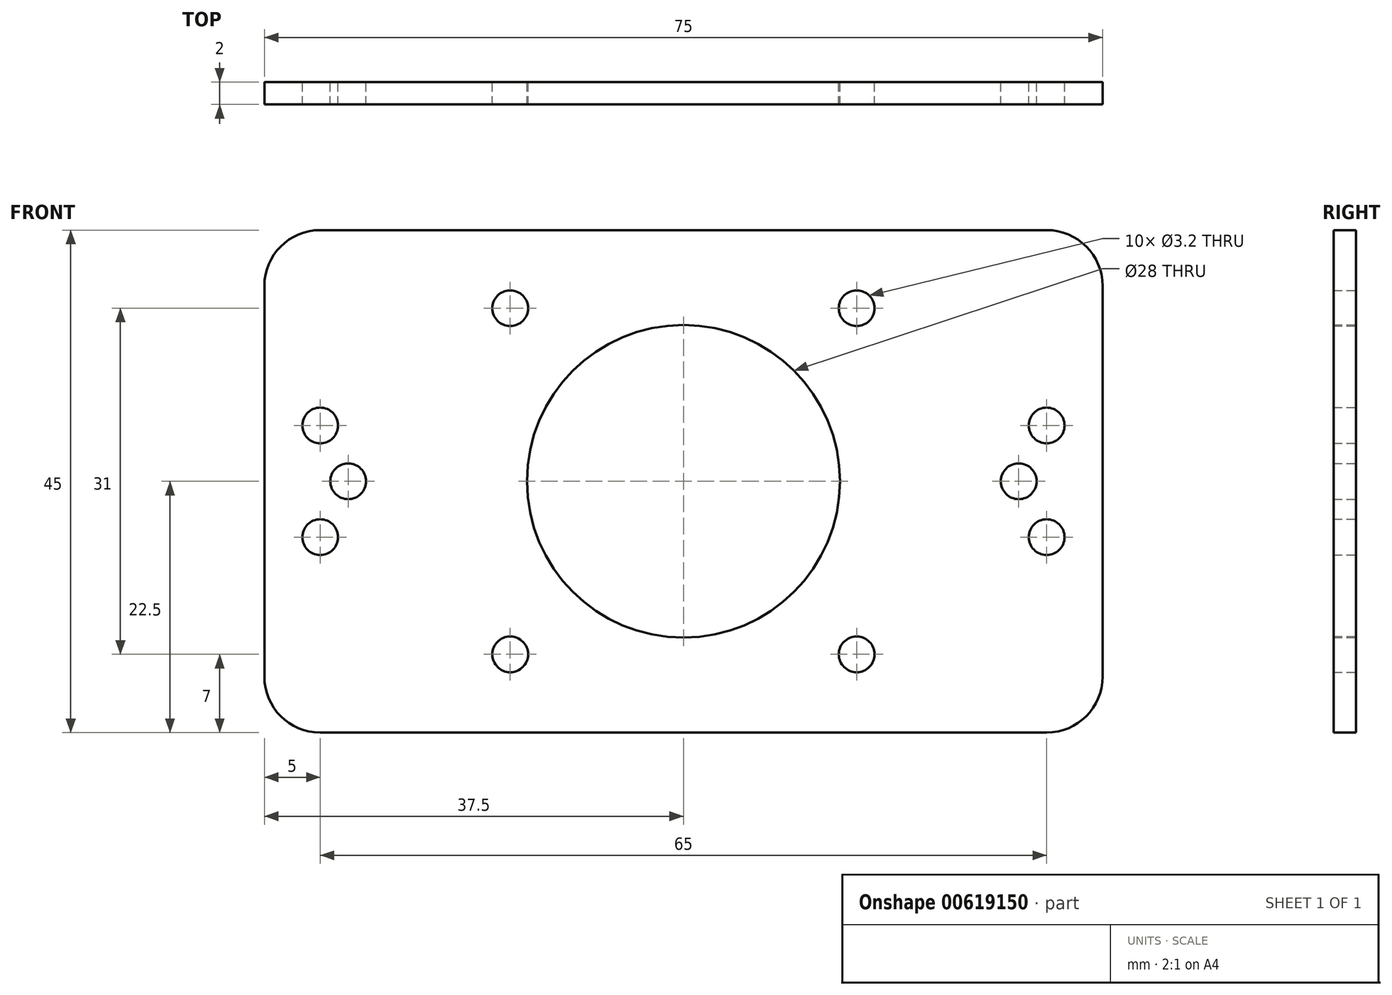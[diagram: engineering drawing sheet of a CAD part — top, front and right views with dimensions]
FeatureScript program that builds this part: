
annotation { "Feature Type Name" : "Feature", "Feature Type Description" : "" }
export const myFeature = defineFeature(function(context is Context, id is Id, definition is map)
    precondition{}
    {
        {
            var Q0;
            Q0=qCreatedBy(makeId("Front.planeOp"),FACE);
            var sketch = newSketch(context, id + "F0", { "sketchPlane" : qUnion([Q0])});
            skLineSegment(sketch, "E0.bottom", {"start": v(5, 0) * mm, "end": v(70, 0) * mm});
            skLineSegment(sketch, "E0.top", {"start": v(5, 45) * mm, "end": v(70, 45) * mm});
            skLineSegment(sketch, "E0.left", {"start": v(0, 5) * mm, "end": v(0, 40) * mm});
            skLineSegment(sketch, "E0.right", {"start": v(75, 5) * mm, "end": v(75, 40) * mm});
            skCircle(sketch, "E1", {"center": v(37.5, 22.5) * mm, "radius": 14 * mm});
            skPoint(sketch, "E1.centerSnap0", {"position": v(75, 22.5) * mm});
            skPoint(sketch, "E1.centerSnap1", {"position": v(37.5, 0) * mm});
            skLineSegment(sketch, "E2", {"start": v(0, 22.5) * mm, "end": v(75, 22.5) * mm, "construction": true});
            skLineSegment(sketch, "E3", {"start": v(37.5, 45) * mm, "end": v(37.5, 0) * mm, "construction": true});
            skCircle(sketch, "E4", {"center": v(22, 38) * mm, "radius": 1.6 * mm});
            skCircle(sketch, "E5.MirrorC", {"center": v(53, 38) * mm, "radius": 1.6 * mm});
            skCircle(sketch, "E6.MirrorC", {"center": v(22, 7) * mm, "radius": 1.6 * mm});
            skCircle(sketch, "E7.MirrorC", {"center": v(53, 7) * mm, "radius": 1.6 * mm});
            skPoint(sketch, "E8.visualSharp", {"position": v(0, 45) * mm});
            skArc(sketch, "E8.filletArc", {"start": v(5, 45) * mm, "mid": v(1.46, 43.54) * mm, "end": v(0, 40) * mm});
            skPoint(sketch, "E9.visualSharp", {"position": v(75, 45) * mm});
            skArc(sketch, "E9.filletArc", {"start": v(75, 40) * mm, "mid": v(73.54, 43.54) * mm, "end": v(70, 45) * mm});
            skPoint(sketch, "E10.visualSharp", {"position": v(75, 0) * mm});
            skArc(sketch, "E10.filletArc", {"start": v(70, 0) * mm, "mid": v(73.54, 1.46) * mm, "end": v(75, 5) * mm});
            skPoint(sketch, "E11.visualSharp", {"position": v(0, 0) * mm});
            skArc(sketch, "E11.filletArc", {"start": v(0, 5) * mm, "mid": v(1.46, 1.46) * mm, "end": v(5, 0) * mm});
            skCircle(sketch, "E12", {"center": v(7.5, 22.5) * mm, "radius": 1.6 * mm});
            skCircle(sketch, "E13", {"center": v(5, 27.5) * mm, "radius": 1.6 * mm});
            skCircle(sketch, "E14.MirrorC", {"center": v(67.5, 22.5) * mm, "radius": 1.6 * mm});
            skCircle(sketch, "E15.MirrorC", {"center": v(70, 27.5) * mm, "radius": 1.6 * mm});
            skCircle(sketch, "E16.MirrorC", {"center": v(5, 17.5) * mm, "radius": 1.6 * mm});
            skCircle(sketch, "E17.MirrorC", {"center": v(70, 17.5) * mm, "radius": 1.6 * mm});
            skSolve(sketch);
        }
        {
            var Q0;
            Q0=makeQuery(id+"F0.imprint","IMPRINT",FACE,{"disambiguationData":[TD([[makeQuery(id+"F0.imprint","IMPRINT",EDGE,{"derivedFrom":sQuery(id+"F0.wireOp",EDGE,"E0.bottom")}),1.0]])]});
            extrude(context, id + "F1", {"entities" : qUnion([Q0]), "depth" : 2 * mm, "offsetDistance" : 25 * mm});
        }
    });
